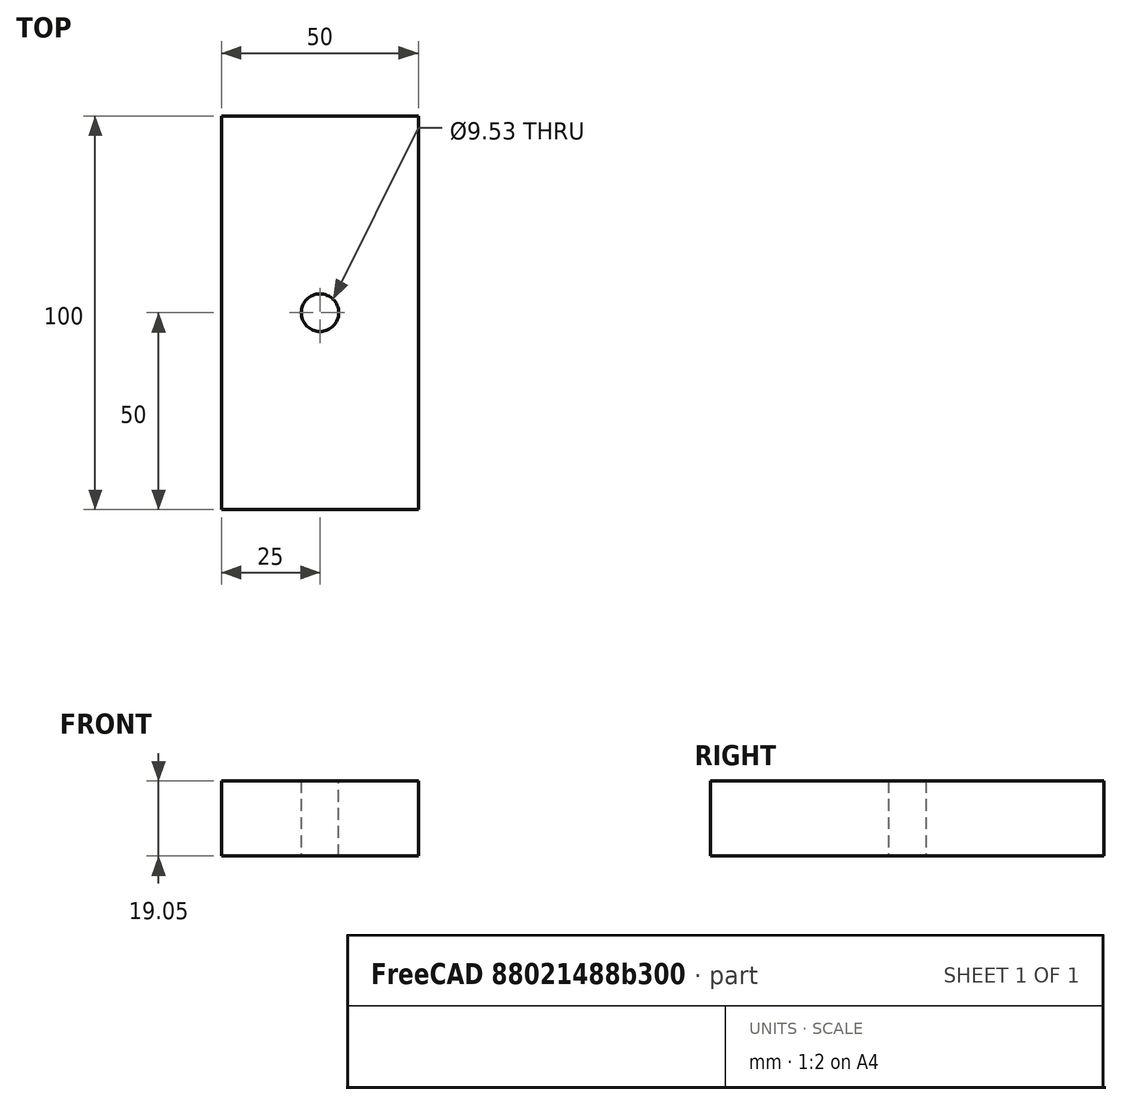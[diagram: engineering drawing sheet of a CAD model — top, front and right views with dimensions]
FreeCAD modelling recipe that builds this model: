
FCSTD DOCUMENT  (FreeCAD 0.19R24291 (Git))
Label: bracket
License: All rights reserved
LicenseURL: http://en.wikipedia.org/wiki/All_rights_reserved
objects: Sketcher::SketchObject×1, PartDesign::Pad×1, PartDesign::Body×1
note: 4 computed .brp shape members not serialized (recipe doc carries the construction recipe); baked Part::Feature solids carry a one-line shape summary decoded from their .brp

FEATURE [Sketcher::SketchObject] Sketch
  FullyConstrained = false
  MapMode = 5
  Support = -> [XY_Plane]
  expr: Constraints[17] = 3 / 8 * 25.4
  sketch-geometry (7):
    g0: LineSegment StartX=0 StartY=0 StartZ=0 EndX=50 EndY=0 EndZ=0
    g1: LineSegment StartX=50 StartY=0 StartZ=0 EndX=50 EndY=100 EndZ=0
    g2: LineSegment StartX=50 StartY=100 StartZ=0 EndX=0 EndY=100 EndZ=0
    g3: LineSegment StartX=0 StartY=100 StartZ=0 EndX=0 EndY=0 EndZ=0
    g4: LineSegment StartX=25 StartY=0 StartZ=0 EndX=25 EndY=66.9946 EndZ=0
    g5: LineSegment StartX=0 StartY=50 StartZ=0 EndX=44.4046 EndY=50 EndZ=0
    g6: Circle CenterX=25 CenterY=50 CenterZ=0 NormalX=0 NormalY=0 NormalZ=1 AngleXU=0 Radius=4.7625
  constraints (18):
    c: Coincident(g0,g1)
    c: Coincident(g1,g2)
    c: Coincident(g2,g3)
    c: Coincident(g3,g0)
    c: Horizontal(g0)
    c: Horizontal(g2)
    c: Vertical(g1)
    c: Vertical(g3)
    c: DistanceX(g0,g0) = 50
    c: DistanceY(g1,g1) = 100
    c: Coincident(g-1,g0)
    c: Vertical(g4)
    c: Horizontal(g5)
    c: Symmetric(g0,g0,g4)
    c: Symmetric(g3,g0,g5)
    c: PointOnObject(g6,g4)
    c: PointOnObject(g6,g5)
    c: Diameter(g6) = 9.525
FEATURE [PartDesign::Pad] Pad
  Direction = (1,1,1)
  Length = 19.05
  Length2 = 100
  Profile = -> Sketch
  Type = 0
  expr: Length = 3 / 4 * 25.4
FEATURE [PartDesign::Body] Body
  Group = -> [Sketch,Pad]
  Origin = -> Origin
  Tip = -> Pad
